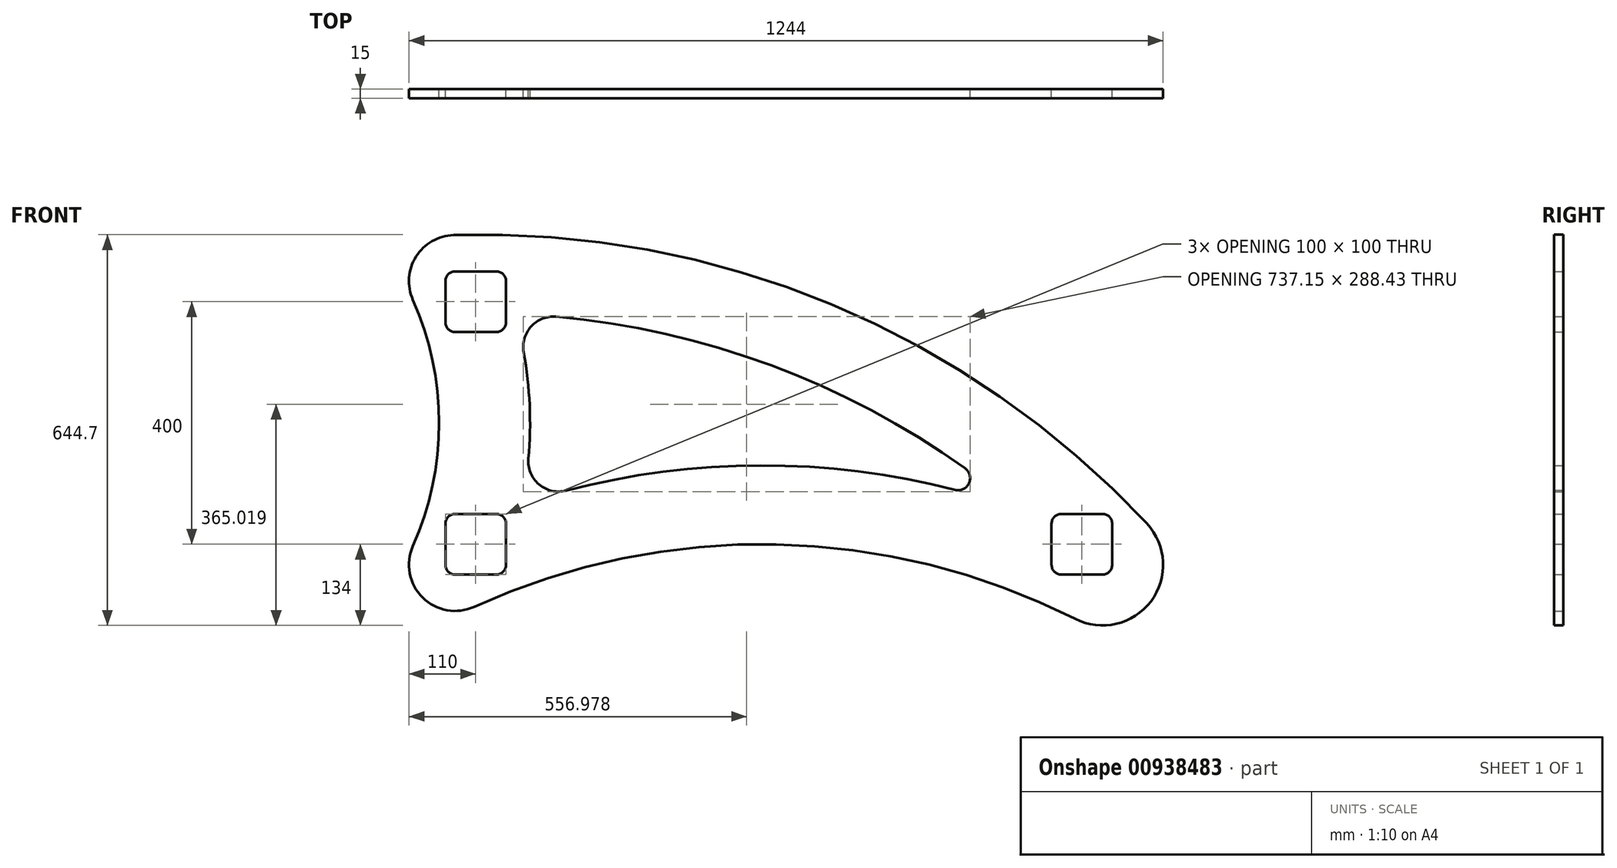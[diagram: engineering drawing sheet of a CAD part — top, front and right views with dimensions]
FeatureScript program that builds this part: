
annotation { "Feature Type Name" : "Feature", "Feature Type Description" : "" }
export const myFeature = defineFeature(function(context is Context, id is Id, definition is map)
    precondition{}
    {
        {
            var Q0;
            Q0=qCreatedBy(makeId("Front.planeOp"),FACE);
            var sketch = newSketch(context, id + "F0", { "sketchPlane" : qUnion([Q0])});
            skLineSegment(sketch, "E0.bottom", {"start": v(34, -50) * mm, "end": v(-34, -50) * mm});
            skLineSegment(sketch, "E0.top", {"start": v(34, 50) * mm, "end": v(-34, 50) * mm});
            skLineSegment(sketch, "E0.left", {"start": v(50, -34) * mm, "end": v(50, 34) * mm});
            skLineSegment(sketch, "E0.right", {"start": v(-50, -34) * mm, "end": v(-50, 34) * mm});
            skPoint(sketch, "E0.middle", {"position": v(0, 0) * mm});
            skPoint(sketch, "E1.visualSharp", {"position": v(-50, 50) * mm});
            skArc(sketch, "E1.filletArc", {"start": v(-34, 50) * mm, "mid": v(-45.31, 45.31) * mm, "end": v(-50, 34) * mm});
            skPoint(sketch, "E2.visualSharp", {"position": v(50, 50) * mm});
            skArc(sketch, "E2.filletArc", {"start": v(50, 34) * mm, "mid": v(45.31, 45.31) * mm, "end": v(34, 50) * mm});
            skPoint(sketch, "E3.visualSharp", {"position": v(50, -50) * mm});
            skArc(sketch, "E3.filletArc", {"start": v(34, -50) * mm, "mid": v(45.31, -45.31) * mm, "end": v(50, -34) * mm});
            skPoint(sketch, "E4.visualSharp", {"position": v(-50, -50) * mm});
            skArc(sketch, "E4.filletArc", {"start": v(-50, -34) * mm, "mid": v(-45.31, -45.31) * mm, "end": v(-34, -50) * mm});
            skPoint(sketch, "E5.0.1.0", {"position": v(50, 350) * mm});
            skPoint(sketch, "E5.0.1.1", {"position": v(-50, 350) * mm});
            skPoint(sketch, "E5.0.1.2", {"position": v(50, 450) * mm});
            skPoint(sketch, "E5.0.1.3", {"position": v(-50, 450) * mm});
            skPoint(sketch, "E5.0.1.4", {"position": v(0, 400) * mm});
            skLineSegment(sketch, "E5.0.1.5", {"start": v(-50, 366) * mm, "end": v(-50, 434) * mm});
            skLineSegment(sketch, "E5.0.1.6", {"start": v(50, 366) * mm, "end": v(50, 434) * mm});
            skLineSegment(sketch, "E5.0.1.7", {"start": v(34, 350) * mm, "end": v(-34, 350) * mm});
            skLineSegment(sketch, "E5.0.1.8", {"start": v(34, 450) * mm, "end": v(-34, 450) * mm});
            skArc(sketch, "E5.0.1.9", {"start": v(-50, 366) * mm, "mid": v(-45.31, 354.69) * mm, "end": v(-34, 350) * mm});
            skArc(sketch, "E5.0.1.10", {"start": v(34, 350) * mm, "mid": v(45.31, 354.69) * mm, "end": v(50, 366) * mm});
            skArc(sketch, "E5.0.1.11", {"start": v(50, 434) * mm, "mid": v(45.31, 445.31) * mm, "end": v(34, 450) * mm});
            skArc(sketch, "E5.0.1.12", {"start": v(-34, 450) * mm, "mid": v(-45.31, 445.31) * mm, "end": v(-50, 434) * mm});
            skLineSegment(sketch, "E5.direction1", {"start": v(-50, -50) * mm, "end": v(1484, -50) * mm, "construction": true});
            skLineSegment(sketch, "E5.direction2", {"start": v(-50, -50) * mm, "end": v(-50, 350) * mm, "construction": true});
            skPoint(sketch, "E6.1.0.0", {"position": v(950, 50) * mm});
            skPoint(sketch, "E6.1.0.1", {"position": v(1050, 50) * mm});
            skPoint(sketch, "E6.1.0.2", {"position": v(950, -50) * mm});
            skPoint(sketch, "E6.1.0.3", {"position": v(1000, 0) * mm});
            skPoint(sketch, "E6.1.0.4", {"position": v(1050, -50) * mm});
            skLineSegment(sketch, "E6.1.0.5", {"start": v(1050, -34) * mm, "end": v(1050, 34) * mm});
            skLineSegment(sketch, "E6.1.0.6", {"start": v(1034, -50) * mm, "end": v(966, -50) * mm});
            skLineSegment(sketch, "E6.1.0.7", {"start": v(1034, 50) * mm, "end": v(966, 50) * mm});
            skLineSegment(sketch, "E6.1.0.8", {"start": v(950, -34) * mm, "end": v(950, 34) * mm});
            skArc(sketch, "E6.1.0.9", {"start": v(1050, 34) * mm, "mid": v(1045.31, 45.31) * mm, "end": v(1034, 50) * mm});
            skArc(sketch, "E6.1.0.10", {"start": v(966, 50) * mm, "mid": v(954.69, 45.31) * mm, "end": v(950, 34) * mm});
            skArc(sketch, "E6.1.0.11", {"start": v(1034, -50) * mm, "mid": v(1045.31, -45.31) * mm, "end": v(1050, -34) * mm});
            skArc(sketch, "E6.1.0.12", {"start": v(950, -34) * mm, "mid": v(954.69, -45.31) * mm, "end": v(966, -50) * mm});
            skLineSegment(sketch, "E6.direction1", {"start": v(-50, -50) * mm, "end": v(950, -50) * mm, "construction": true});
            skArc(sketch, "E7", {"start": v(-36.38, 509.96) * mm, "mid": v(-98.37, 474.4) * mm, "end": v(-103.45, 403.12) * mm});
            skArc(sketch, "E8", {"start": v(-103.45, -3.13) * mm, "mid": v(-60.33, 200) * mm, "end": v(-103.45, 403.12) * mm});
            skArc(sketch, "E9", {"start": v(1107.1, 34.24) * mm, "mid": v(586.75, 395.62) * mm, "end": v(-36.38, 509.96) * mm});
            skArc(sketch, "E10", {"start": v(988.86, -123.23) * mm, "mid": v(495.48, -0.23) * mm, "end": v(-2.47, -103.15) * mm});
            skLineSegment(sketch, "E11", {"start": v(0, 0) * mm, "end": v(1000, 0) * mm, "construction": true});
            skArc(sketch, "E12.trimOffspring", {"start": v(-103.45, -3.13) * mm, "mid": v(-87.48, -88) * mm, "end": v(-2.47, -103.15) * mm});
            skArc(sketch, "E13.trimOffspring", {"start": v(988.86, -123.23) * mm, "mid": v(1113.96, -94.05) * mm, "end": v(1107.1, 34.24) * mm});
            skArc(sketch, "E14.trimOffspring", {"start": v(893.22, 58.47) * mm, "mid": v(850.9, 92.7) * mm, "end": v(807.26, 125.23) * mm, "construction": true});
            skArc(sketch, "E15.trimOffspring", {"start": v(893.22, 58.47) * mm, "mid": v(842.26, 75.11) * mm, "end": v(790.63, 89.6) * mm, "construction": true});
            skArc(sketch, "E16.trimOffspring", {"start": v(87.02, 141.31) * mm, "mid": v(89.02, 229.16) * mm, "end": v(79.15, 316.47) * mm});
            skPoint(sketch, "E17.visualSharp", {"position": v(64.36, 379.64) * mm});
            skArc(sketch, "E17.filletArc", {"start": v(132.8, 375.23) * mm, "mid": v(91.42, 359.15) * mm, "end": v(79.15, 316.47) * mm});
            skPoint(sketch, "E18.visualSharp", {"position": v(75.87, 66.76) * mm});
            skArc(sketch, "E18.filletArc", {"start": v(87.02, 141.31) * mm, "mid": v(104.5, 98.64) * mm, "end": v(149.48, 88.43) * mm});
            skArc(sketch, "E19", {"start": v(790.63, 89.6) * mm, "mid": v(813.76, 100.5) * mm, "end": v(807.26, 125.23) * mm});
            skArc(sketch, "E20", {"start": v(807.26, 125.23) * mm, "mid": v(486.73, 295.29) * mm, "end": v(132.8, 375.23) * mm});
            skArc(sketch, "E21", {"start": v(790.63, 89.6) * mm, "mid": v(469.98, 130) * mm, "end": v(149.48, 88.43) * mm});
            skSolve(sketch);
        }
        {
            var Q0;
            Q0 = qSketchRegion(id + "F0", true);
            extrude(context, id + "F1", {"entities" : qUnion([Q0]), "depth" : 15 * mm, "offsetDistance" : 25 * mm});
        }
    });
